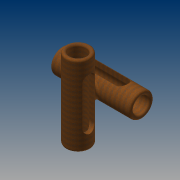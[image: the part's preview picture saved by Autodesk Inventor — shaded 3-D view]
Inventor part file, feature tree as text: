
AUTODESK INVENTOR PART (.ipt)
format: ipt  version: 2014 (Build 180170000, 170)  size: 283,648 bytes
history: native  units: mm
features: extrude x5, sketch x5, fillet x3, plane x3
ambient origin geometry x8: Origin, YZ Plane, XZ Plane, XY Plane, X Axis, Y Axis, Z Axis, Center Point
bodies: Solid1 (feature_tree)
feature tree (16):
  extrude  "Extrusion1"  Depth=40.0mm
  fillet  "Fillet1"  Radius=200.0mm
  plane  "Work Plane1"
  extrude  "Extrusion2"  Depth=30.0mm
  plane  "Work Plane2"
  extrude  "Extrusion3"  Depth=15.0mm
  extrude  "Extrusion4"  Depth=150.0mm TaperAngle=0.0deg
  fillet  "Fillet2"  Radius=30.0mm
  plane  "Work Plane3"
  extrude  "Extrusion5"  Depth=100.0mm
  fillet  "Fillet3"  Radius=10.0mm
  sketch  "Sketch1"  dims[d0=60.0mm d1=40.0mm d2=200.0mm d3=0.0mm]
  sketch  "Sketch2"  dims[d4=5.0mm d5=30.0mm]
  sketch  "Sketch3"  dims[d6=100.0mm d7=15.0mm]
  sketch  "Sketch4"  dims[d8=100.0mm d9=150.0mm d10=0.0mm d11=30.0mm]
  sketch  "Sketch5"  dims[d12=40.0mm d13=100.0mm d14=10.0mm d15=0.0mm d16=10.0mm d17=0.0mm d18=60.0mm d19=40.0mm d21=30.0mm d22=200.0mm d23=0.0mm d24=5.0mm d25=100.0mm d26=100.0mm d27=15.0mm d28=30.0mm d29=100.0mm d30=200.0mm d31=0.0mm d32=5.0mm]
